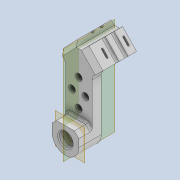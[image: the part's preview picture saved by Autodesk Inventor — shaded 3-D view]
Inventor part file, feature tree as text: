
AUTODESK INVENTOR PART (.ipt)
format: ipt  version: 2020 (Build 240168000, 168)  size: 443,904 bytes
history: native  units: mm
features: extrude x13, sketch x13, projected_geometry x10, thicken_offset x7, chamfer x4, fillet x4, other x4, plane x2, mirror x2, reference x2
ambient origin geometry x8: Origin, YZ Plane, XZ Plane, XY Plane, X Axis, Y Axis, Z Axis, Center Point
bodies: Solid1 (feature_tree)
feature tree (61):
  extrude  "Extrusion1"  Depth=6.0mm
  extrude  "Extrusion2"  Depth=10.0mm TaperAngle=0.0deg
  chamfer  "Chamfer1"  Distance=6.0mm
  extrude  "Extrusion3"  Depth=6.0mm TaperAngle=0.0deg
  extrude  "Extrusion4"  Depth=4.0mm
  extrude  "Extrusion5"  Depth=4.0mm
  thicken_offset  "Thicken1"
  thicken_offset  "Thicken2"
  extrude  "Extrusion6"  Depth=15.0mm TaperAngle=0.0deg
  extrude  "Extrusion7"  Depth=1.0mm
  chamfer  "Chamfer2"  Distance=15.0mm
  extrude  "Extrusion8"  Depth=15.0mm TaperAngle=0.0deg
  plane  "Work Plane2"
  mirror  "Mirror2"
  thicken_offset  "Thicken3"
  thicken_offset  "Thicken4"
  fillet  "Fillet2"  Radius=2.0mm
  fillet  "Fillet3"  Radius=15.0mm
  extrude  "Extrusion9"  Depth=1.0mm
  mirror  "Mirror3"
  fillet  "Fillet4"  Radius=1.0mm
  plane  "Work Plane3"
  extrude  "Extrusion10"  Depth=2.0mm
  chamfer  "Chamfer3"  Distance=2.0mm
  thicken_offset  "Thicken5"
  extrude  "Extrusion11"  Depth=3.0mm
  fillet  "Fillet5"  Radius=3.0mm
  chamfer  "Chamfer4"  Distance=1.5mm
  thicken_offset  "Thicken6"
  thicken_offset  "Thicken7"
  extrude  "Extrusion12"  Depth=10.0mm
  extrude  "Extrusion13"  Depth=10.0mm
  sketch  "Sketch1"  dims[d0=6.0mm d1=30.0mm]
  sketch  "Sketch2"  dims[d2=12.0mm d3=10.0mm d4=0.0mm]
  projected_geometry  "Projected Loop1"
  sketch  "Sketch3"  dims[d5=13.0mm]
  projected_geometry  "Projected Loop2"
  sketch  "Sketch4"  dims[d6=27.0mm d7=6.0mm d8=0.0mm]
  projected_geometry  "Projected Loop3"
  reference  "Reference1"
  sketch  "Sketch5"  dims[d9=3.0mm d10=2.0mm d11=45.0deg d12=6.0mm d13=0.0mm]
  projected_geometry  "Projected Loop4"
  sketch  "Sketch6"  dims[d14=10.0mm d15=4.0mm]
  sketch  "Sketch7"  dims[d16=10.0mm d17=4.0mm]
  sketch  "Sketch8"  dims[d18=15.0mm d19=0.0mm d20=15.0mm d21=0.0mm]
  reference  "Reference2"
  projected_geometry  "Projected Loop5"
  sketch  "Sketch9"  dims[d22=1.0mm d23=1.0mm]
  projected_geometry  "Projected Loop6"
  projected_geometry  "Projected Loop7"
  sketch  "Sketch10"  dims[d24=1.0mm]
  sketch  "Sketch11"  dims[d25=1.0mm]
  projected_geometry  "Projected Loop8"
  sketch  "Sketch12"  dims[d27=2.5mm d28=15.0mm d29=0.0mm]
  projected_geometry  "Projected Loop9"
  sketch  "Sketch13"  dims[d30=2.5mm d31=15.0mm d32=0.0mm d33=2.0mm d34=2.0mm d35=45.0deg d36=15.0mm d37=0.0mm d38=1.0mm d39=1.0mm d40=2.0mm d41=2.0mm d42=3.0mm d43=3.0mm d44=1.5mm d45=0.7mm d46=9.5mm d47=1.5mm d48=0.7mm d49=15.0mm d50=0.0mm d51=2.0mm d52=-2.0mm d53=1.0mm d54=6.0mm d55=0.0mm d56=1.0mm d57=2.0mm d58=45.0deg d59=1.0mm d60=1.0mm d61=5.0mm d62=6.0mm d63=12.0mm d64=3.0mm d65=3.0mm d66=3.0mm d67=3.0mm d68=3.0mm d69=3.0mm d70=3.0mm d71=6.0mm d72=0.0mm d73=1.0mm d74=0.5mm d75=2.0mm d76=45.0deg d77=0.05mm d78=0.05mm d79=0.05mm d80=0.05mm d81=1.5mm d82=1.5mm d83=10.0mm d84=0.0mm d85=1.5mm d86=1.5mm d87=10.0mm d88=0.0mm]
  projected_geometry  "Projected Loop10"
  parser-record x1  (decoder bookkeeping rows leaked as tree rows — omitted from the tree; the rows remain in map.json)
  other  "driver_ass_1.iam"
  other  "driver_wheel_1:1"
  other  "driver_wheel_1:2"
note: 1 file-system path scrubbed to <path> (originals preserved in map.json)
